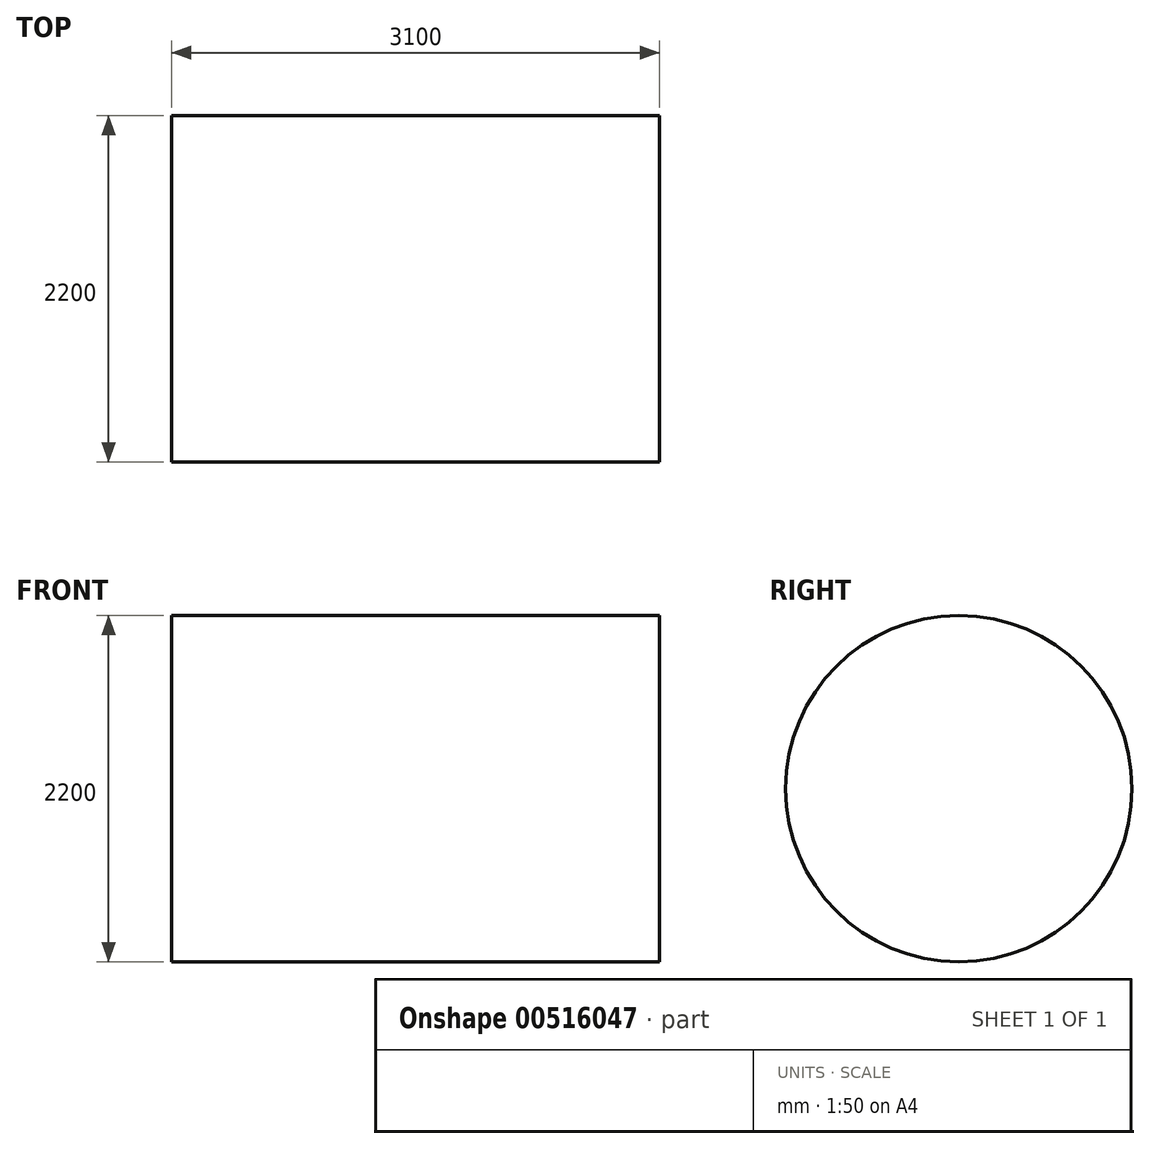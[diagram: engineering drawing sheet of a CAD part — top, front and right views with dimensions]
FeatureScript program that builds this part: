
annotation { "Feature Type Name" : "Feature", "Feature Type Description" : "" }
export const myFeature = defineFeature(function(context is Context, id is Id, definition is map)
    precondition{}
    {
        {
            var Q0;
            Q0=qCreatedBy(makeId("Right.planeOp"),FACE);
            var sketch = newSketch(context, id + "F0", { "sketchPlane" : qUnion([Q0])});
            skCircle(sketch, "E0", {"center": v(0, 0) * mm, "radius": 1100 * mm});
            skSolve(sketch);
        }
        {
            var Q0;
            Q0 = qSketchRegion(id + "F0", true);
            var Q1;
            Q1=sQuery(id+"F0.wireOp",EDGE,"E0");
            extrude(context, id + "F1", {"entities" : qUnion([Q0]), "bodyType" : ToolBodyType.SURFACE, "surfaceEntities" : qUnion([Q1]), "endBound" : BoundingType.SYMMETRIC, "depth" : 3100 * mm, "offsetDistance" : 25 * mm});
        }
    });
